# Revit family: prevedo_ILUTEX
name_source: partatom
category: Leuchten
revit_build: Autodesk Revit 2018 (Build: 20190510_1515(x64)
units: mm (PartAtom-declared; Revit-internal decimal feet)

## family parameters
Basisbauteil = Fläche
Beim Laden mit Abzugskörper schneiden = Ja
Bemaßung runder Anschluss = Durchmesser verwenden
Gemeinsam genutzt = Nein
Lichtquelle = Ja
OmniClass-Nummer = 23.80.70.00
OmniClass-Titel = Lighting
Raumberechnungspunkt = Nein
Teiletyp = Normal

## types (3) — shared parameters
12 Volt = Ja
24 Volt = Nein
Ausbildung Leuchtmittel = LED
Ausführungsunterlagen = gemäß Zeichnung und Einzelbeschreibung
B_Rahmen Dicke l/r = 4 mm  [stored 0.0131234 ft]
B_Rahmen Dicke o/u = 4 mm  [stored 0.0131234 ft]
Bauelement = Leuchte
Bauteil, Leuchte/Lampe = Anbauleuchte
Dimmbarkeit Leuchte = elektronisch dimmbar
Energieeffizienzklasse = A+
Farbfilter = 16777215
Farbtemperaturverschiebung bei Dämpfen der Lampe = <Keine Auswahl>
Gewicht = ca. 5kg/m²
Größe des Lichtquellensymbols = 500 mm  [stored 1.64042 ft]
Hersteller = prevedo Lichtmedien GmbH
Intensität = 10000 lm/m²
Lampe = LED
Lebensdauer h Leuchtmittel = mind. 50000
Leuchte Bauweise = Abdeckung aus Stoff
Material Abdeckung = Stoff_leuchtend
Produktinformationen = https://www.prevedo.de
Schaltungsweise = Betriebsgerät elektronisch
Spannung = 12 V
Typenkommentare = Bei 230V Zuleitung ist ein Trafo notwendig. Dieser und weiteres Zubehör ist separat erhältlich.
URL = https://www.prevedo.de
Umgebungstemperatur = -15°C bis +40°C
Vorgabe-Ansicht = 1219 mm
Werkstoff, Gehäuse = Aluminium
zB01_min = 200 mm  [stored 0.656168 ft]
zL01_min = 200 mm  [stored 0.656168 ft]
zero-valued in all types: B_Versatz Einfügepos, B_check_error

## per-type parameters (varying)
| type | Anwendung | B_Last_frame | B_Last_star | B_check_area | B_frame | B_shape_rechteckig | B_shape_rund-oval | Beschreibung | Breite | Dicke (nicht editierbar) | Laenge | Leistung W Leuchtmittel | Scheinlast | Schutzart | zB01 | zB01_max | zD01 | zL01 | zL01_max |
| ILUTEX frame | Ein effizientes Multitalent ist unser extrem flaches Rahmensystem ILUTEX frame ganz nach Wunschgröße. Ob als großformatiges Einzel-Leuchtbild oder als paneliertes Gesamtbild über eine Wand von 30 m Länge – ILUTEX frame zieht die Blicke auf sich. Damit eignet es sich für die Foyergestaltung genauso wie für die Präsentation auf einer Messe oder die eindrucksvolle Bebilderung einer Ausstellung. | 32 VA | 120 VA | 0.8 m² | Ja | Ja | Nein | Das einzelne Sichtmaß von bis zu 1,2 x 2,5 m garantiert großen kreativen Freiraum und hohe Aufmerksamkeit. Bei fast randloser Optik und homogener Ausleuchtung wirkt ILUMAG frame stets elegant und souverän. Dabei ist das System sehr leicht – auch mehrteilig – zu installieren. Mit einer Bauhöhe von nur 20 mm kann es ggf. auch direkt in eine Trockenbauwand bündig eingelassen werden, ohne dass der schnelle Bildwechsel mittels eines gekederten Textildisplays eingeschränkt wird. | 800 mm  [stored 2.62467 ft] | 20 mm  [stored 0.0656168 ft] | 1000 mm  [stored 3.28084 ft] | 32 W | 32 VA | staubgeschützt, angenähert an IP22 | 800 mm  [stored 2.62467 ft] | 1200 mm | 20 mm  [stored 0.0656168 ft] | 1000 mm  [stored 3.28084 ft] | 2500 mm  [stored 8.2021 ft] |
| ILUTEX star_rechteckig | ILUTEX star verkörpert ein Konzept zum Realisieren besonders flacher, gleichmäßig leuchtender Decken oder Wände in großen Räumen, wie z.B. Hotellobbys oder Wellness-Oasen. Mit einer Lösung, die – ausgehend von handhab- und verbindbaren LED-Modulen – durchgängige Leuchtpanele von bis zu 20 m² ermöglichen, ist eine breite Anwendungspalette gegeben. Dadurch, dass die Flächen nicht zwingend rechteckig, sondern auch andere Formen besitzen können, wird die Palette zusätzlich erweitert. | 64 VA | 480 VA | 3 m² | Nein | Ja | Nein | Unter Einsatz von 45 oder 60 mm flachen Alu-Kederprofilen entstehen in Verbindung mit LED-Panelen auf Alu-Dibond-Trägern Leuchtpanele mit Farbtemperatur nach Bedarf (von festem Weiß, über steuerbares Weiß bis RBGW). Diese werden nacheinander mit Schrauben an der Wand oder der Decke montiert, an die entsprechenden Trafos und Controller angeschlossen und letztlich mit einem kompletten Textilschirm überspannt. Sie erfüllen strenge Brandschutzvorschriften, sind energieeffizient und unterstützen zudem die Schalldämmung im Raum. Optional sind die Leuchtschirme bedruckbar. | 1500 mm  [stored 4.92126 ft] | 45 mm  [stored 0.147638 ft] | 2000 mm  [stored 6.56168 ft] | 480 W | 480 VA | spritzwassergeschützt, angenähert an IP44 | 1500 mm  [stored 4.92126 ft] | 3000 mm  [stored 9.84252 ft] | 45 mm  [stored 0.147638 ft] | 2000 mm  [stored 6.56168 ft] | 9000 mm |
| ILUTEX star_oval/rund | ILUTEX star verkörpert ein Konzept zum Realisieren besonders flacher, gleichmäßig leuchtender Decken oder Wände in großen Räumen, wie z.B. Hotellobbys oder Wellness-Oasen. Mit einer Lösung, die – ausgehend von handhab- und verbindbaren LED-Modulen – durchgängige Leuchtpanele von bis zu 20 m² ermöglichen, ist eine breite Anwendungspalette gegeben. Dadurch, dass die Flächen nicht zwingend rechteckig, sondern auch andere Formen besitzen können, wird die Palette zusätzlich erweitert. | 0 VA | 720 VA | 4 m² | Nein | Nein | Ja | Unter Einsatz von 45 oder 60 mm flachen Alu-Kederprofilen entstehen in Verbindung mit LED-Panelen auf Alu-Dibond-Trägern Leuchtpanele mit Farbtemperatur nach Bedarf (von festem Weiß, über steuerbares Weiß bis RBGW). Diese werden nacheinander mit Schrauben an der Wand oder der Decke montiert, an die entsprechenden Trafos und Controller angeschlossen und letztlich mit einem kompletten Textilschirm überspannt. Sie erfüllen strenge Brandschutzvorschriften, sind energieeffizient und unterstützen zudem die Schalldämmung im Raum. Optional sind die Leuchtschirme bedruckbar. | 2000 mm  [stored 6.56168 ft] | 45 mm  [stored 0.147638 ft] | 2000 mm  [stored 6.56168 ft] | 720 W | 720 VA | spritzwassergeschützt, angenähert an IP44 | 2000 mm  [stored 6.56168 ft] | 3000 mm  [stored 9.84252 ft] | 45 mm  [stored 0.147638 ft] | 2000 mm  [stored 6.56168 ft] | 9000 mm |

note: column(s) folded — value = type name in every type: Modell

note: [stored X ft] marks values corroborated as IEEE doubles in the binary element streams (Revit-internal decimal feet)
